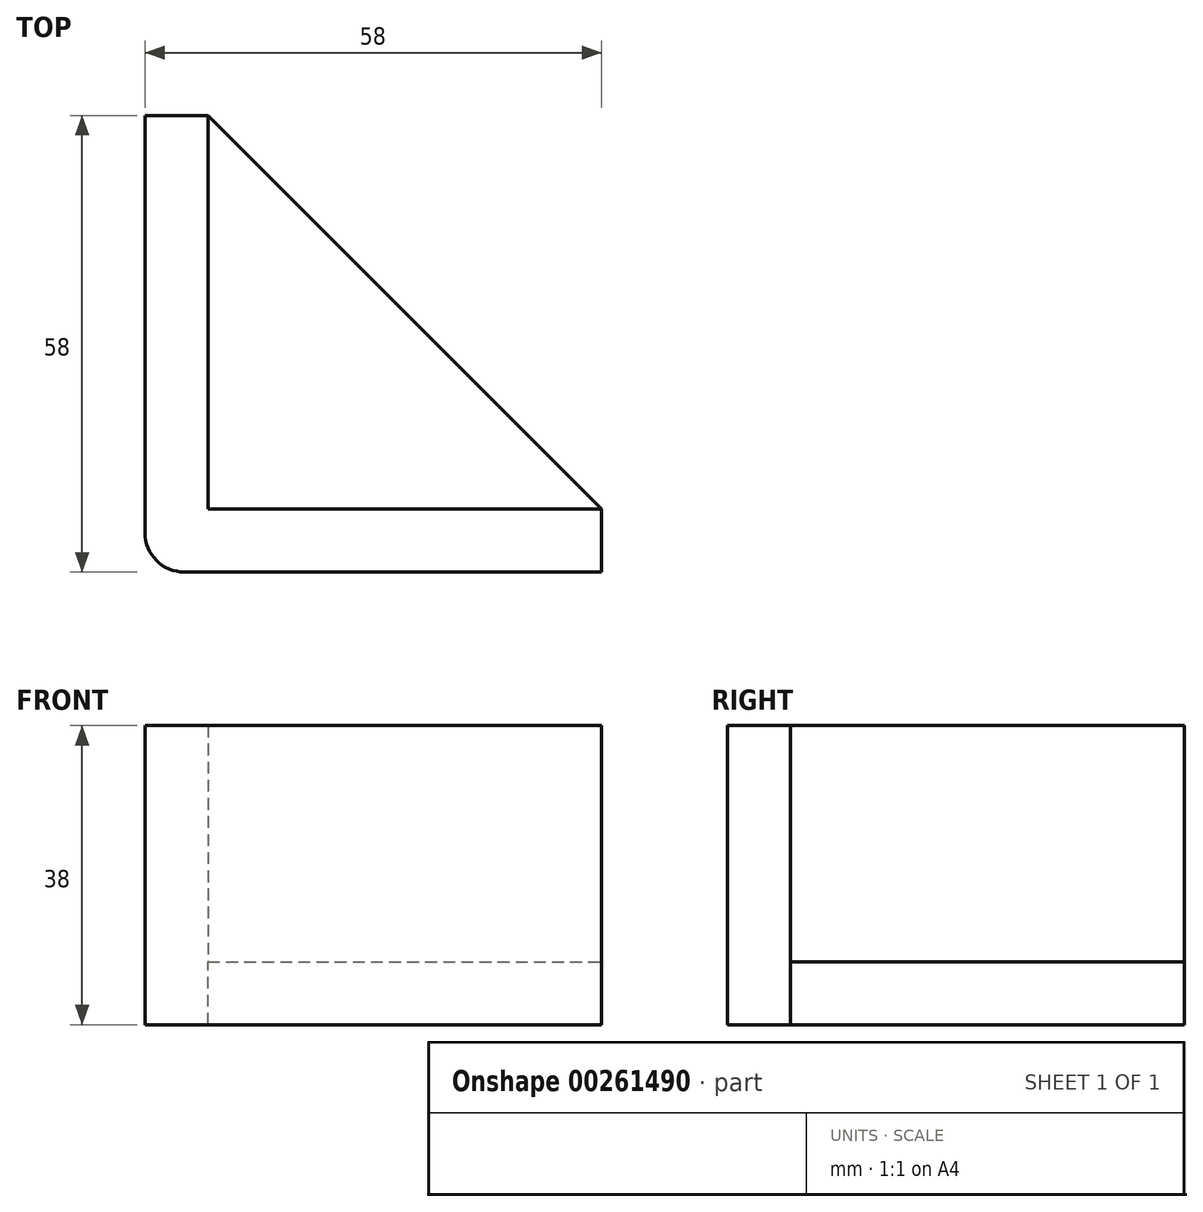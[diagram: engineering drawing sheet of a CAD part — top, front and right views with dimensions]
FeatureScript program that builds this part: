
annotation { "Feature Type Name" : "Feature", "Feature Type Description" : "" }
export const myFeature = defineFeature(function(context is Context, id is Id, definition is map)
    precondition{}
    {
        {
            var Q0;
            Q0=qCreatedBy(makeId("Top.planeOp"),FACE);
            var sketch = newSketch(context, id + "F0", { "sketchPlane" : qUnion([Q0])});
            skLineSegment(sketch, "E0.bottom", {"start": v(29, -29) * mm, "end": v(-29, -29) * mm});
            skLineSegment(sketch, "E0.top", {"start": v(29, 29) * mm, "end": v(-29, 29) * mm});
            skLineSegment(sketch, "E0.left", {"start": v(29, -29) * mm, "end": v(29, 29) * mm});
            skLineSegment(sketch, "E0.right", {"start": v(-29, -29) * mm, "end": v(-29, 29) * mm});
            skPoint(sketch, "E0.middle", {"position": v(0, 0) * mm});
            skSolve(sketch);
        }
        {
            var Q0;
            Q0 = qSketchRegion(id + "F0", true);
            extrude(context, id + "F1", {"entities" : qUnion([Q0]), "depth" : 8 * mm});
        }
        {
            var Q0;
            Q0=makeQuery(id+"F1.opExtrude","CAP_FACE",FACE,{"disambiguationData":[OSD([sQuery(id+"F0.wireOp",EDGE,"E0.bottom"),sQuery(id+"F0.wireOp",EDGE,"E0.top"),sQuery(id+"F0.wireOp",EDGE,"E0.left"),sQuery(id+"F0.wireOp",EDGE,"E0.right")])],"isStart":false});
            var sketch = newSketch(context, id + "F2", { "sketchPlane" : qUnion([Q0])});
            skLineSegment(sketch, "E1.0", {"start": v(-29, -29) * mm, "end": v(-29, 29) * mm});
            skLineSegment(sketch, "E1.1", {"start": v(29, -29) * mm, "end": v(-29, -29) * mm});
            skLineSegment(sketch, "E2.0", {"start": v(-21, -21) * mm, "end": v(-21, 29) * mm});
            skLineSegment(sketch, "E2.1", {"start": v(29, -21) * mm, "end": v(-21, -21) * mm});
            skLineSegment(sketch, "E3", {"start": v(-29, 29) * mm, "end": v(-21, 29) * mm});
            skLineSegment(sketch, "E4", {"start": v(29, -29) * mm, "end": v(29, -21) * mm});
            skSolve(sketch);
        }
        {
            var Q0;
            Q0 = qSketchRegion(id + "F2", true);
            extrude(context, id + "F3", {"entities" : qUnion([Q0]), "operationType" : NewBodyOperationType.ADD, "depth" : 30 * mm});
        }
        {
            var Q0;
            Q0=makeQuery(id+"F1.opExtrude","CAP_FACE",FACE,{"disambiguationData":[OSD([sQuery(id+"F0.wireOp",EDGE,"E0.bottom"),sQuery(id+"F0.wireOp",EDGE,"E0.top"),sQuery(id+"F0.wireOp",EDGE,"E0.left"),sQuery(id+"F0.wireOp",EDGE,"E0.right")])],"isStart":false});
            var sketch = newSketch(context, id + "F4", { "sketchPlane" : qUnion([Q0])});
            skLineSegment(sketch, "E5", {"start": v(-21, 29) * mm, "end": v(29, -21) * mm});
            skLineSegment(sketch, "E6.0", {"start": v(29, 29) * mm, "end": v(-21, 29) * mm});
            skLineSegment(sketch, "E6.1", {"start": v(29, -21) * mm, "end": v(29, 29) * mm});
            skSolve(sketch);
        }
        {
            var Q0;
            Q0 = qSketchRegion(id + "F4", true);
            extrude(context, id + "F5", {"entities" : qUnion([Q0]), "operationType" : NewBodyOperationType.REMOVE, "endBound" : BoundingType.THROUGH_ALL, "oppositeDirection" : true, "depth" : 25 * mm});
        }
        {
            var Q0;
            Q0=makeQuery(id+"F3.boolean.opBoolean","MERGE",EDGE,{"derivedFrom":[makeQuery(id+"F1.opExtrude","SWEPT_EDGE",EDGE,{"disambiguationData":[OSD([sQuery(id+"F0.wireOp",EDGE,"E0.bottom"),sQuery(id+"F0.wireOp",EDGE,"E0.right")])]}),makeQuery(id+"F3.opExtrude","SWEPT_EDGE",EDGE,{"disambiguationData":[OSD([sQuery(id+"F2.wireOp",EDGE,"E1.0"),sQuery(id+"F2.wireOp",EDGE,"E1.1")])]})]});
            fillet(context, id + "F6", {"entities" : qUnion([Q0]), "radius" : 5 * mm, "tangentPropagation" : true, "allowEdgeOverflow" : false});
        }
    });
